# Revit family: Sanitary_Dispensers_Slits_Soap-Dispenser
name_source: partatom
category: Furniture
units: mm (PartAtom-declared; Revit-internal decimal feet)

## family parameters
Always vertical = No
Cut with Voids When Loaded = No
OmniClass Number = 23.40.20.00
OmniClass Title = General Furniture and Specialties
Room Calculation Point = No
Shared = No
Work Plane-Based = Yes

## types (1)
- Slits Manual Soap Alcogel refillable Dispenser two arms
    AssetType = Fixed
    BIMObjectName = Sanitary_Dispensers_Slits_Soap-Dispenser
    Brand = Svedholm
    Color = Various
    Cost = 0 $
    Default Elevation = 1219 mm
    Description = Alcogel/soap dispenser made of powder coated steel. All colours are available upon request. Refillable dispenser 1000 ml.
The entire SLITS collection is approved by the Swedish BYGGVARUBEDÖMNINGEN and assessed in SundaHus Material Data.
    DurationUnit = Year
    IfcExportAs = IfcFurnishingElementType
    IfcExportType = MIRROR
    MainColor = White
    Manufacturer = Svedholm
    ManufacturerName = Svedholm
    ManufacturerURL = https://www.svedholm.se
    Material = Metal and mirror
    MirrorMainMaterial = RAL 7021
    Model = Slits Manual Soap Alcogel refillable Dispenser two arms
    ModelNumber = 410.600.024
    NBSDescription = Mirrors
    NBSReference = 45-35-72/336
    Name = Slits_Soap-Dispenser
    NominalDepth = 112 mm
    NominalHeight = 398 mm
    NominalLength = 110 mm
    ProductInformation = Alcogel/soap dispenser made of powder coated steel. All colours are available upon request. Refillable dispenser 1000 ml.
The entire SLITS collection is approved by the Swedish BYGGVARUBEDÖMNINGEN and assessed in SundaHus Material Data.
    Shape = Sculptured
    Size = 300/390 x110x110 mm
    URL = https://www.svedholm.se
    Uniclass2 = Pr_40_70_22_81
    Uniclass2015Description = Soap dispensers
    Uniclass2015Reference = Pr_40_70_22_81
    Version = 1
    VersionDate = 06/07/2023
    WarrantyDurationUnit = Years

## geometry (parser evidence)
native form markers: Sweep x5
no freeform markers — native parametric forms only
